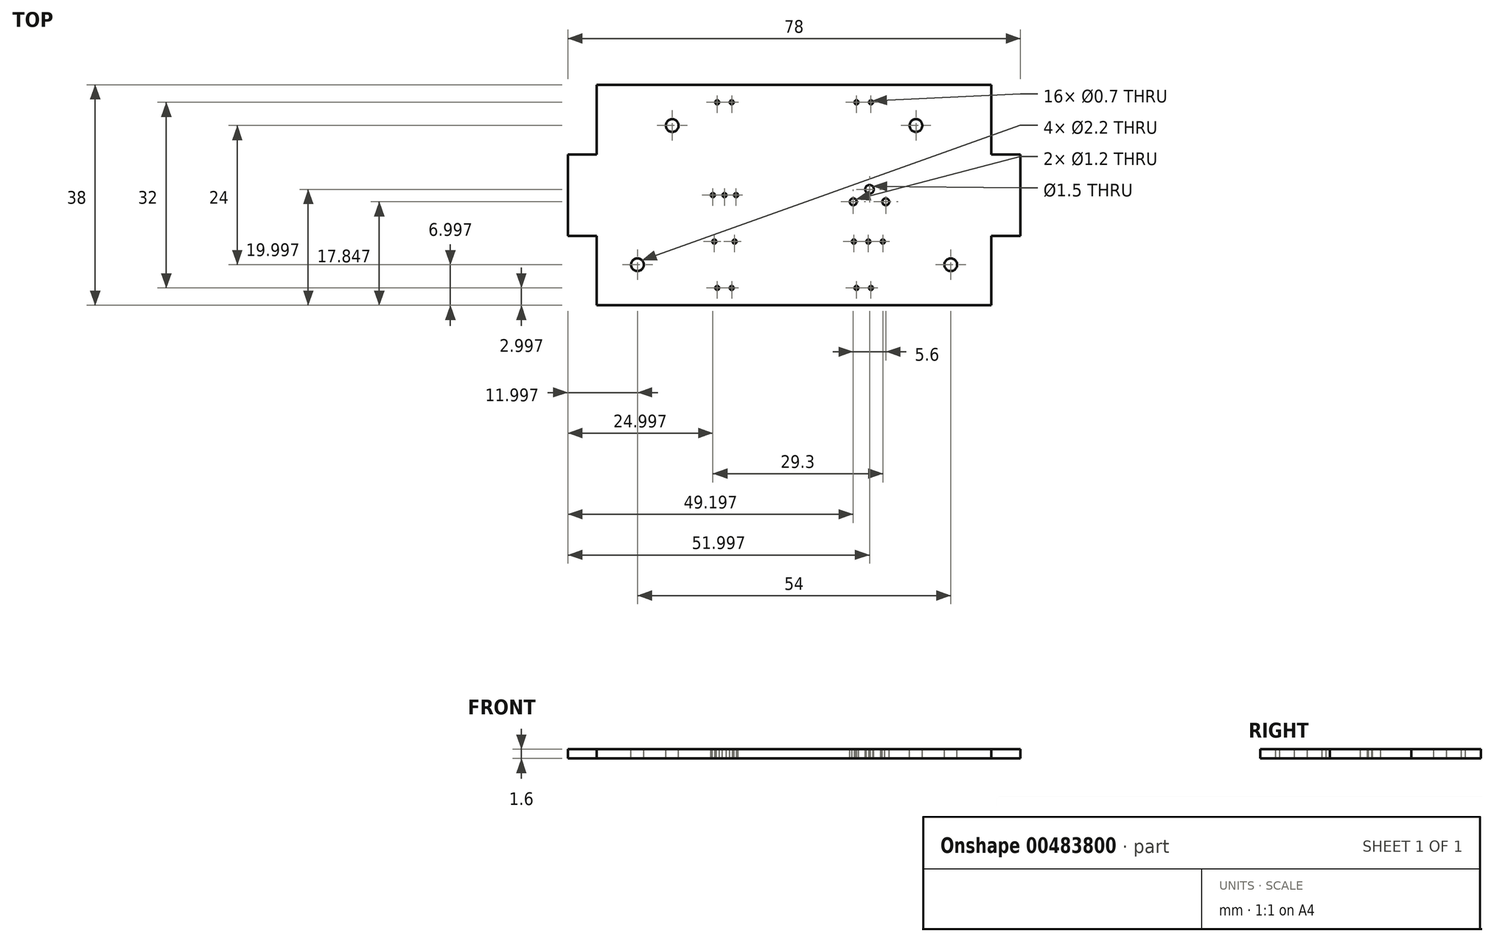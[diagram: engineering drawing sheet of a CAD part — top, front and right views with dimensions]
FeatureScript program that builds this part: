
annotation { "Feature Type Name" : "Feature", "Feature Type Description" : "" }
export const myFeature = defineFeature(function(context is Context, id is Id, definition is map)
    precondition{}
    {
        {
            var Q0;
            Q0=qCreatedBy(makeId("Top.planeOp"),FACE);
            var sketch = newSketch(context, id + "F0", { "sketchPlane" : qUnion([Q0])});
            skLineSegment(sketch, "E0", {"start": v(41.32, 33.2) * mm, "end": v(41.32, -3.8) * mm, "construction": true});
            skLineSegment(sketch, "E1.bottom", {"start": v(7.32, -4.3) * mm, "end": v(75.32, -4.3) * mm});
            skLineSegment(sketch, "E1.top", {"start": v(7.32, 33.7) * mm, "end": v(75.32, 33.7) * mm});
            skLineSegment(sketch, "E1.left", {"start": v(7.32, -4.3) * mm, "end": v(7.32, 33.7) * mm});
            skLineSegment(sketch, "E1.right", {"start": v(75.32, -4.3) * mm, "end": v(75.32, 33.7) * mm});
            skPoint(sketch, "E1.middle", {"position": v(41.32, 14.7) * mm});
            skLineSegment(sketch, "E2.bottom", {"start": v(80.32, 21.7) * mm, "end": v(2.32, 21.7) * mm});
            skLineSegment(sketch, "E2.top", {"start": v(80.32, 7.7) * mm, "end": v(2.32, 7.7) * mm});
            skLineSegment(sketch, "E2.left", {"start": v(80.32, 21.7) * mm, "end": v(80.32, 7.7) * mm});
            skLineSegment(sketch, "E2.right", {"start": v(2.32, 21.7) * mm, "end": v(2.32, 7.7) * mm});
            skSolve(sketch);
        }
        {
            var Q0;
            Q0=qSketchRegion(id+"F0",true);
            extrude(context, id + "F1", {"entities" : qUnion([Q0]), "depth" : 1.6 * mm});
        }
        {
            var Q0;
            Q0=makeQuery(id+"F1.opExtrude","CAP_FACE",FACE,{"disambiguationData":[OSD([sQuery(id+"F0.wireOp",EDGE,"E1.bottom"),sQuery(id+"F0.wireOp",EDGE,"E1.top"),sQuery(id+"F0.wireOp",EDGE,"E1.left"),sQuery(id+"F0.wireOp",EDGE,"E1.right")])],"isStart":false});
            var sketch = newSketch(context, id + "F2", { "sketchPlane" : qUnion([Q0])});
            skCircle(sketch, "E3", {"center": v(27.32, 14.7) * mm, "radius": 0.35 * mm});
            skLineSegment(sketch, "E4", {"start": v(41.32, 22.32) * mm, "end": v(41.32, 29.29) * mm, "construction": true});
            skCircle(sketch, "E5.1.0.0", {"center": v(29.32, 14.7) * mm, "radius": 0.35 * mm});
            skLineSegment(sketch, "E5.direction1", {"start": v(27.32, 14.7) * mm, "end": v(29.32, 14.7) * mm, "construction": true});
            skCircle(sketch, "E6.0.2.0", {"center": v(31.32, 14.7) * mm, "radius": 0.35 * mm});
            skLineSegment(sketch, "E7", {"start": v(28.32, 14.7) * mm, "end": v(2.32, 14.7) * mm, "construction": true});
            skSolve(sketch);
        }
        {
            var Q0;
            Q0=makeQuery(id+"F1.opExtrude","CAP_FACE",FACE,{"disambiguationData":[OSD([sQuery(id+"F0.wireOp",EDGE,"E1.bottom"),sQuery(id+"F0.wireOp",EDGE,"E1.top"),sQuery(id+"F0.wireOp",EDGE,"E1.left"),sQuery(id+"F0.wireOp",EDGE,"E1.right")])],"isStart":false});
            var sketch = newSketch(context, id + "F3", { "sketchPlane" : qUnion([Q0])});
            skLineSegment(sketch, "E8", {"start": v(54.32, 14.1) * mm, "end": v(54.32, 27.42) * mm, "construction": true});
            skLineSegment(sketch, "E9", {"start": v(41.32, 6.29) * mm, "end": v(41.32, 24.04) * mm, "construction": true});
            skLineSegment(sketch, "E10", {"start": v(51.17, 13.55) * mm, "end": v(51.87, 13.55) * mm, "construction": true});
            skLineSegment(sketch, "E11", {"start": v(51.52, 13.55) * mm, "end": v(51.52, 23.97) * mm, "construction": true});
            skLineSegment(sketch, "E12", {"start": v(53.82, 15.7) * mm, "end": v(54.82, 15.7) * mm, "construction": true});
            skLineSegment(sketch, "E13", {"start": v(54.32, 19.92) * mm, "end": v(54.32, 15.7) * mm, "construction": true});
            skArc(sketch, "E14.0.startCap", {"start": v(53.82, 15.45) * mm, "mid": v(53.57, 15.7) * mm, "end": v(53.82, 15.95) * mm});
            skArc(sketch, "E14.0.endCap", {"start": v(54.82, 15.95) * mm, "mid": v(55.07, 15.7) * mm, "end": v(54.82, 15.45) * mm});
            skLineSegment(sketch, "E14.0.left", {"start": v(53.82, 15.95) * mm, "end": v(54.82, 15.95) * mm});
            skLineSegment(sketch, "E14.0.right", {"start": v(53.82, 15.45) * mm, "end": v(54.82, 15.45) * mm});
            skLineSegment(sketch, "E15", {"start": v(50.5, 14.7) * mm, "end": v(53.65, 14.7) * mm, "construction": true});
            skArc(sketch, "E16.0.startCap", {"start": v(51.87, 13.8) * mm, "mid": v(52.12, 13.55) * mm, "end": v(51.87, 13.3) * mm});
            skArc(sketch, "E16.0.endCap", {"start": v(51.17, 13.3) * mm, "mid": v(50.92, 13.55) * mm, "end": v(51.17, 13.8) * mm});
            skLineSegment(sketch, "E16.0.left", {"start": v(51.17, 13.3) * mm, "end": v(51.87, 13.3) * mm});
            skLineSegment(sketch, "E16.0.right", {"start": v(51.17, 13.8) * mm, "end": v(51.87, 13.8) * mm});
            skArc(sketch, "E17.MirrorCS", {"start": v(57.47, 13.3) * mm, "mid": v(57.72, 13.55) * mm, "end": v(57.47, 13.8) * mm});
            skLineSegment(sketch, "E18.MirrorCS", {"start": v(57.47, 13.3) * mm, "end": v(56.77, 13.3) * mm});
            skLineSegment(sketch, "E19.MirrorCS", {"start": v(57.47, 13.8) * mm, "end": v(56.77, 13.8) * mm});
            skArc(sketch, "E20.MirrorCS", {"start": v(56.77, 13.8) * mm, "mid": v(56.52, 13.55) * mm, "end": v(56.77, 13.3) * mm});
            skLineSegment(sketch, "E21", {"start": v(50.5, 14.7) * mm, "end": v(2.32, 14.7) * mm, "construction": true});
            skCircle(sketch, "E22", {"center": v(51.52, 13.55) * mm, "radius": 0.6 * mm});
            skCircle(sketch, "E23", {"center": v(54.32, 15.7) * mm, "radius": 0.75 * mm});
            skCircle(sketch, "E24", {"center": v(57.12, 13.55) * mm, "radius": 0.6 * mm});
            skPoint(sketch, "E24.centerSnap0", {"position": v(57.12, 13.3) * mm});
            skSolve(sketch);
        }
        {
            var Q0;
            Q0=makeQuery(id+"F1.opExtrude","CAP_FACE",FACE,{"disambiguationData":[OSD([sQuery(id+"F0.wireOp",EDGE,"E1.bottom"),sQuery(id+"F0.wireOp",EDGE,"E1.top"),sQuery(id+"F0.wireOp",EDGE,"E1.left"),sQuery(id+"F0.wireOp",EDGE,"E1.right")])],"isStart":false});
            var sketch = newSketch(context, id + "F4", { "sketchPlane" : qUnion([Q0])});
            skCircle(sketch, "E25", {"center": v(51.62, 6.7) * mm, "radius": 0.35 * mm});
            skCircle(sketch, "E26.1.0.0", {"center": v(56.62, 6.7) * mm, "radius": 0.35 * mm});
            skLineSegment(sketch, "E26.direction1", {"start": v(51.62, 6.7) * mm, "end": v(56.62, 6.7) * mm, "construction": true});
            skLineSegment(sketch, "E27", {"start": v(41.32, 6.29) * mm, "end": v(41.32, 17.65) * mm, "construction": true});
            skLineSegment(sketch, "E28", {"start": v(54.12, 6.7) * mm, "end": v(54.12, 23.7) * mm, "construction": true});
            skCircle(sketch, "E29", {"center": v(54.12, 6.7) * mm, "radius": 0.35 * mm});
            skLineSegment(sketch, "E30", {"start": v(2.32, 14.7) * mm, "end": v(80.32, 14.7) * mm, "construction": true});
            skSolve(sketch);
        }
        {
            var Q0;
            Q0=makeQuery(id+"F1.opExtrude","CAP_FACE",FACE,{"disambiguationData":[OSD([sQuery(id+"F0.wireOp",EDGE,"E1.bottom"),sQuery(id+"F0.wireOp",EDGE,"E1.top"),sQuery(id+"F0.wireOp",EDGE,"E1.left"),sQuery(id+"F0.wireOp",EDGE,"E1.right")])],"isStart":false});
            var sketch = newSketch(context, id + "F5", { "sketchPlane" : qUnion([Q0])});
            skCircle(sketch, "E31", {"center": v(28.07, -1.3) * mm, "radius": 0.35 * mm});
            skCircle(sketch, "E32.1.0.0", {"center": v(30.57, -1.3) * mm, "radius": 0.35 * mm});
            skLineSegment(sketch, "E32.direction1", {"start": v(28.07, -1.3) * mm, "end": v(30.57, -1.3) * mm, "construction": true});
            skLineSegment(sketch, "E33", {"start": v(29.32, -1.3) * mm, "end": v(29.32, 26.14) * mm, "construction": true});
            skLineSegment(sketch, "E34", {"start": v(41.32, 33.7) * mm, "end": v(41.32, -4.3) * mm, "construction": true});
            skCircle(sketch, "E35.MirrorC", {"center": v(52.07, -1.3) * mm, "radius": 0.35 * mm});
            skCircle(sketch, "E36.MirrorC", {"center": v(54.57, -1.3) * mm, "radius": 0.35 * mm});
            skLineSegment(sketch, "E37", {"start": v(2.32, 14.7) * mm, "end": v(80.32, 14.7) * mm, "construction": true});
            skCircle(sketch, "E38.MirrorC", {"center": v(54.57, 30.7) * mm, "radius": 0.35 * mm});
            skCircle(sketch, "E39.MirrorC", {"center": v(52.07, 30.7) * mm, "radius": 0.35 * mm});
            skCircle(sketch, "E40.MirrorC", {"center": v(30.57, 30.7) * mm, "radius": 0.35 * mm});
            skCircle(sketch, "E41.MirrorC", {"center": v(28.07, 30.7) * mm, "radius": 0.35 * mm});
            skSolve(sketch);
        }
        {
            var Q0;
            Q0=makeQuery(id+"F1.opExtrude","CAP_FACE",FACE,{"disambiguationData":[OSD([sQuery(id+"F0.wireOp",EDGE,"E1.bottom"),sQuery(id+"F0.wireOp",EDGE,"E1.top"),sQuery(id+"F0.wireOp",EDGE,"E1.left"),sQuery(id+"F0.wireOp",EDGE,"E1.right")])],"isStart":false});
            var sketch = newSketch(context, id + "F6", { "sketchPlane" : qUnion([Q0])});
            skCircle(sketch, "E42", {"center": v(27.57, 6.7) * mm, "radius": 0.35 * mm});
            skCircle(sketch, "E43.1.0.0", {"center": v(31.07, 6.7) * mm, "radius": 0.35 * mm});
            skLineSegment(sketch, "E43.direction1", {"start": v(27.57, 6.7) * mm, "end": v(31.07, 6.7) * mm, "construction": true});
            skLineSegment(sketch, "E44", {"start": v(29.32, 13.4) * mm, "end": v(29.32, 6.7) * mm, "construction": true});
            skLineSegment(sketch, "E45", {"start": v(2.32, 14.7) * mm, "end": v(80.32, 14.7) * mm, "construction": true});
            skSolve(sketch);
        }
        {
            var Q0;
            Q0=qSketchRegion(id+"F4",true);
            var Q1;
            Q1=qSketchRegion(id+"F5",true);
            var Q2;
            Q2=qSketchRegion(id+"F6",true);
            var Q3;
            Q3=qSketchRegion(id+"F3",true);
            var Q4;
            Q4=qSketchRegion(id+"F2",true);
            extrude(context, id + "F7", {"entities" : qUnion([Q0, Q1, Q2, Q3, Q4]), "operationType" : NewBodyOperationType.REMOVE, "oppositeDirection" : true, "depth" : 4 * mm});
        }
        {
            var Q0;
            Q0=makeQuery(id+"F1.opExtrude","CAP_FACE",FACE,{"disambiguationData":[OSD([sQuery(id+"F0.wireOp",EDGE,"E1.bottom"),sQuery(id+"F0.wireOp",EDGE,"E1.top"),sQuery(id+"F0.wireOp",EDGE,"E1.left"),sQuery(id+"F0.wireOp",EDGE,"E1.right")])],"isStart":false});
            var sketch = newSketch(context, id + "F8", { "sketchPlane" : qUnion([Q0])});
            skLineSegment(sketch, "E46", {"start": v(41.32, 33.7) * mm, "end": v(41.32, -4.3) * mm, "construction": true});
            skCircle(sketch, "E47", {"center": v(62.32, 26.7) * mm, "radius": 1.1 * mm});
            skCircle(sketch, "E48.MirrorC", {"center": v(20.32, 26.7) * mm, "radius": 1.1 * mm});
            skLineSegment(sketch, "E49", {"start": v(41.32, 14.7) * mm, "end": v(80.32, 14.7) * mm, "construction": true});
            skCircle(sketch, "E50", {"center": v(68.32, 2.7) * mm, "radius": 1.1 * mm});
            skCircle(sketch, "E51.MirrorC", {"center": v(14.32, 2.7) * mm, "radius": 1.1 * mm});
            skSolve(sketch);
        }
        {
            var Q0;
            Q0=qSketchRegion(id+"F8",true);
            extrude(context, id + "F9", {"entities" : qUnion([Q0]), "operationType" : NewBodyOperationType.REMOVE, "oppositeDirection" : true, "depth" : 25 * mm});
        }
    });
